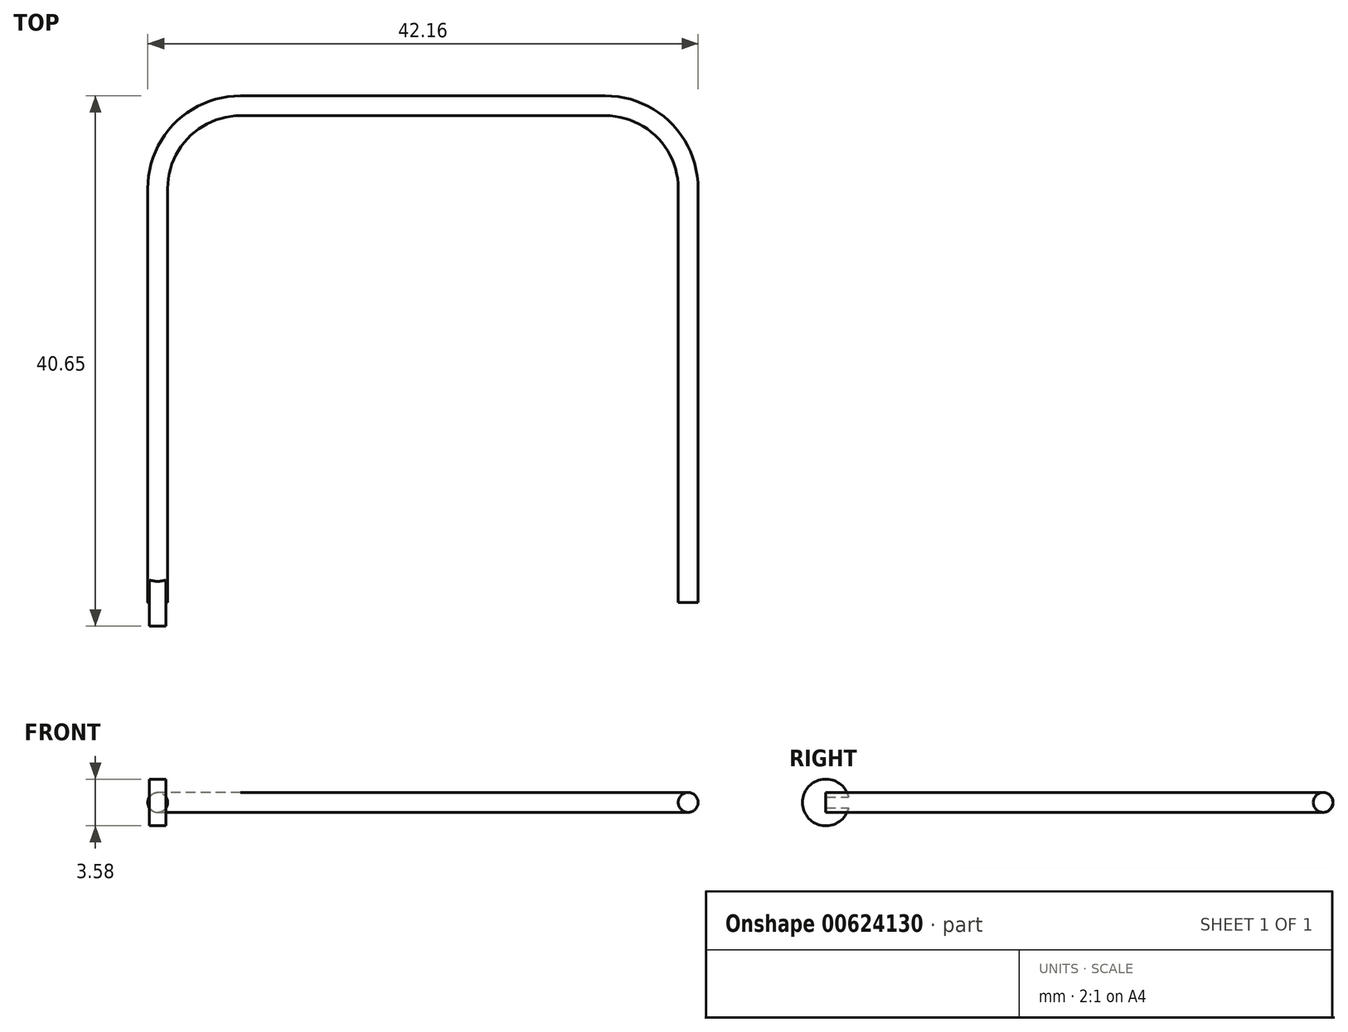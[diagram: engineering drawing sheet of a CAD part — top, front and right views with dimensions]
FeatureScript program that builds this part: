
annotation { "Feature Type Name" : "Feature", "Feature Type Description" : "" }
export const myFeature = defineFeature(function(context is Context, id is Id, definition is map)
    precondition{}
    {
        {
            var Q0;
            Q0=qCreatedBy(makeId("Top.planeOp"),FACE);
            var sketch = newSketch(context, id + "F0", { "sketchPlane" : qUnion([Q0])});
            skLineSegment(sketch, "E0", {"start": v(-25.9, 52.54) * mm, "end": v(-53.85, 52.54) * mm});
            skLineSegment(sketch, "E1", {"start": v(-60.2, 46.2) * mm, "end": v(-60.2, 14.44) * mm});
            skPoint(sketch, "E2.visualSharp", {"position": v(-60.2, 52.54) * mm});
            skArc(sketch, "E2.filletArc", {"start": v(-53.85, 52.54) * mm, "mid": v(-58.34, 50.68) * mm, "end": v(-60.2, 46.2) * mm});
            skPoint(sketch, "E3.visualSharp", {"position": v(-19.56, 52.54) * mm});
            skArc(sketch, "E3.filletArc", {"start": v(-19.56, 46.2) * mm, "mid": v(-21.42, 50.68) * mm, "end": v(-25.9, 52.54) * mm});
            skLineSegment(sketch, "E4.trimOffspring", {"start": v(-19.56, 14.44) * mm, "end": v(-19.56, 46.2) * mm});
            skSolve(sketch);
        }
        {
            var Q0;
            Q0=qCreatedBy(makeId("Front.planeOp"),FACE);
            cPlane(context, id + "F1", {"entities" : qUnion([Q0]), "cplaneType" : CPlaneType.OFFSET, "offset" : 6.82 * mm, "oppositeDirection" : true, "width" : 152.4 * mm, "height" : 152.4 * mm});
        }
        {
            var Q0;
            Q0=qCreatedBy(id+"F1.planeOp",FACE);
            cPlane(context, id + "F2", {"entities" : qUnion([Q0]), "cplaneType" : CPlaneType.OFFSET, "offset" : 7.62 * mm, "oppositeDirection" : true, "width" : 152.4 * mm, "height" : 152.4 * mm});
        }
        {
            var Q0;
            Q0=qCreatedBy(id+"F2.planeOp",FACE);
            var sketch = newSketch(context, id + "F3", { "sketchPlane" : qUnion([Q0])});
            skCircle(sketch, "E5", {"center": v(-60.2, 0) * mm, "radius": 0.76 * mm});
            skPoint(sketch, "E6", {"position": v(-60.1, 0) * mm});
            skSolve(sketch);
        }
        {
            var Q0;
            Q0=makeQuery(id+"F3.imprint","IMPRINT",FACE,{"disambiguationData":[TD([[makeQuery(id+"F3.imprint","IMPRINT",EDGE,{"derivedFrom":sQuery(id+"F3.wireOp",EDGE,"E5")}),1.0]])]});
            var Q1;
            Q1=sQuery(id+"F0.wireOp",EDGE,"E1");
            var Q2;
            Q2=sQuery(id+"F0.wireOp",EDGE,"E2.filletArc");
            var Q3;
            Q3=sQuery(id+"F0.wireOp",EDGE,"E0");
            var Q4;
            Q4=sQuery(id+"F0.wireOp",EDGE,"E3.filletArc");
            var Q5;
            Q5=sQuery(id+"F0.wireOp",EDGE,"E4.trimOffspring");
            sweep(context, id + "F4", {"profiles" : qUnion([Q0]), "path" : qUnion([Q1, Q2, Q3, Q4, Q5])});
        }
        {
            var Q0;
            Q0=qCreatedBy(makeId("Right.planeOp"),FACE);
            cPlane(context, id + "F5", {"entities" : qUnion([Q0]), "cplaneType" : CPlaneType.OFFSET, "offset" : 60.2 * mm, "oppositeDirection" : true, "width" : 152.4 * mm, "height" : 152.4 * mm});
        }
        {
            var Q0;
            Q0=qCreatedBy(id+"F5.planeOp",FACE);
            var sketch = newSketch(context, id + "F6", { "sketchPlane" : qUnion([Q0])});
            skCircle(sketch, "E7", {"center": v(14.44, 0) * mm, "radius": 1.8 * mm});
            skSolve(sketch);
        }
        {
            var Q0;
            Q0=makeQuery(id+"F6.imprint","IMPRINT",FACE,{"disambiguationData":[TD([[makeQuery(id+"F6.imprint","IMPRINT",EDGE,{"derivedFrom":sQuery(id+"F6.wireOp",EDGE,"E7")}),1.0]])]});
            extrude(context, id + "F7", {"entities" : qUnion([Q0]), "operationType" : NewBodyOperationType.ADD, "endBound" : BoundingType.SYMMETRIC, "depth" : 1.27 * mm, "offsetDistance" : 25.4 * mm});
        }
    });
